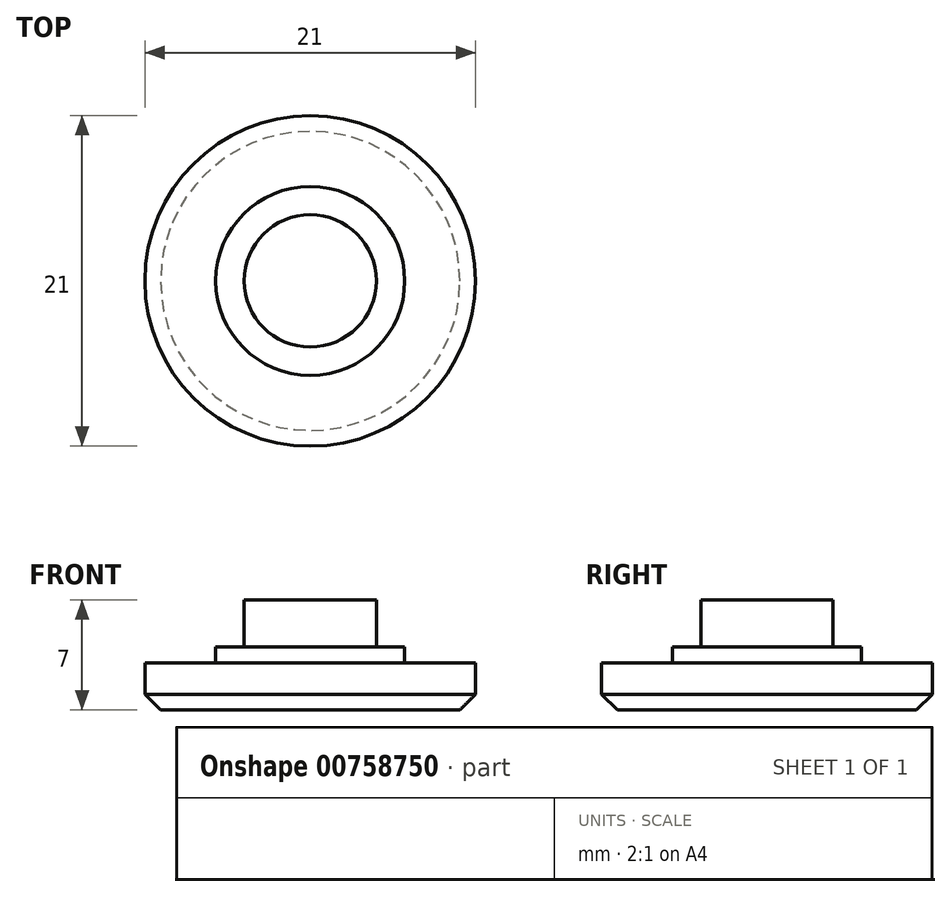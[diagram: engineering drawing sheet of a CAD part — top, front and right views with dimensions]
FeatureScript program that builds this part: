
annotation { "Feature Type Name" : "Feature", "Feature Type Description" : "" }
export const myFeature = defineFeature(function(context is Context, id is Id, definition is map)
    precondition{}
    {
        {
            assignVariable(context, id + "F0", {"name" : "clearance", "anyValue" : 1});
        }
        {
            assignVariable(context, id + "F1", {"name" : "capthick", "anyValue" : 3});
        }
        {
            var Q0;
            Q0=qCreatedBy(makeId("Top.planeOp"),FACE);
            var sketch = newSketch(context, id + "F2", { "sketchPlane" : qUnion([Q0])});
            skCircle(sketch, "E0", {"center": v(0, 0) * mm, "radius": 4.2 * mm});
            skCircle(sketch, "E1", {"center": v(0, 0) * mm, "radius": 6 * mm});
            skCircle(sketch, "E2", {"center": v(0, 0) * mm, "radius": 10.5 * mm});
            skSolve(sketch);
        }
        {
            var Q0;
            Q0=makeQuery(id+"F2.imprint","IMPRINT",FACE,{"disambiguationData":[TD([[makeQuery(id+"F2.imprint","IMPRINT",EDGE,{"derivedFrom":sQuery(id+"F2.wireOp",EDGE,"E1")}),-1.0]])]});
            extrude(context, id + "F3", {"entities" : qUnion([Q0]), "depth" : (getVariable(context, 'capthick')) * mm, "offsetDistance" : 25 * mm});
        }
        {
            var Q0;
            Q0=makeQuery(id+"F2.imprint","IMPRINT",FACE,{"disambiguationData":[TD([[makeQuery(id+"F2.imprint","IMPRINT",EDGE,{"derivedFrom":sQuery(id+"F2.wireOp",EDGE,"E0")}),-1.0]])]});
            extrude(context, id + "F4", {"entities" : qUnion([Q0]), "operationType" : NewBodyOperationType.ADD, "depth" : (getVariable(context, 'clearance') + getVariable(context, 'capthick')) * mm, "offsetDistance" : 25 * mm});
        }
        {
            var Q0;
            Q0=makeQuery(id+"F2.imprint","IMPRINT",FACE,{"disambiguationData":[TD([[makeQuery(id+"F2.imprint","IMPRINT",EDGE,{"derivedFrom":sQuery(id+"F2.wireOp",EDGE,"E0")}),1.0]])]});
            extrude(context, id + "F5", {"entities" : qUnion([Q0]), "operationType" : NewBodyOperationType.ADD, "depth" : (getVariable(context, 'clearance') + getVariable(context, 'capthick') + 3) * mm, "offsetDistance" : 25 * mm});
        }
        {
            var Q0;
            Q0=makeQuery(id+"F3.opExtrude","CAP_EDGE",EDGE,{"disambiguationData":[OSD([sQuery(id+"F2.wireOp",EDGE,"E2")])],"isStart":true});
            chamfer(context, id + "F6", {"entities" : qUnion([Q0]), "width" : 1 * mm, "tangentPropagation" : true});
        }
    });
